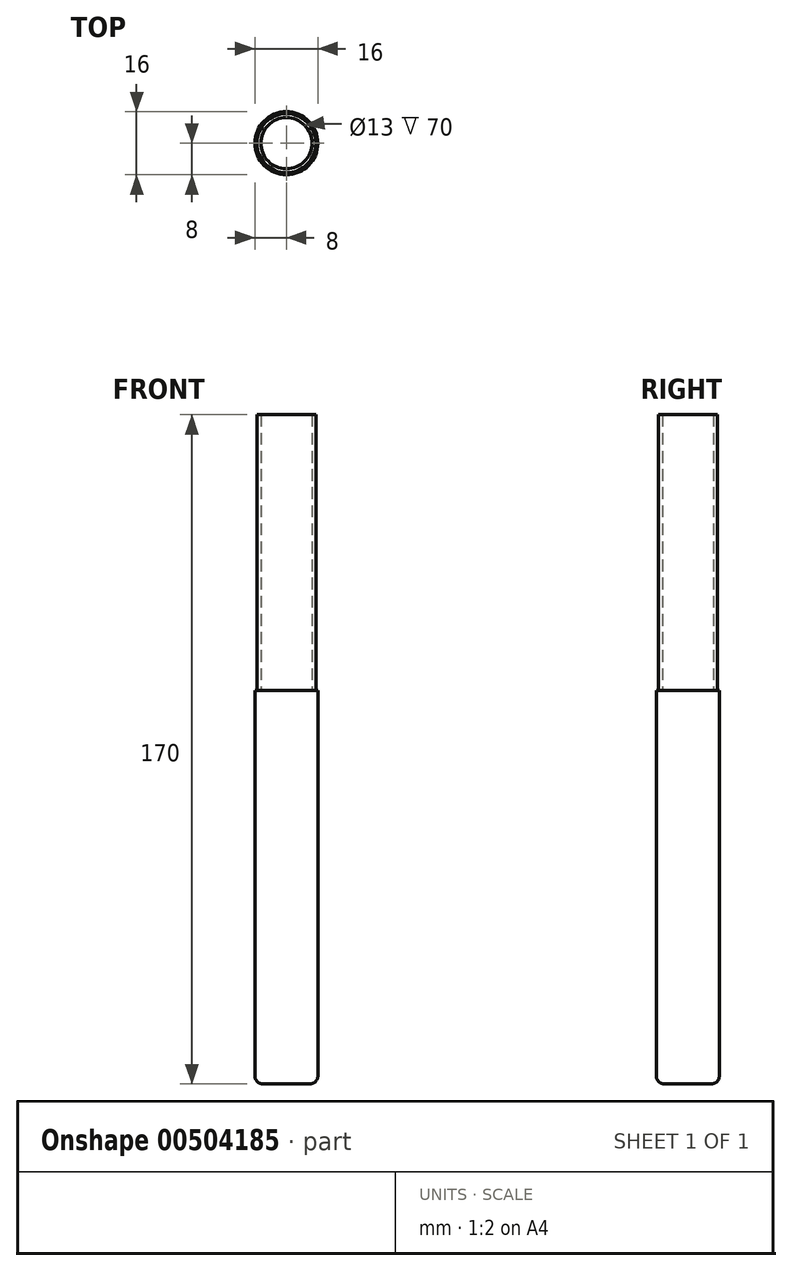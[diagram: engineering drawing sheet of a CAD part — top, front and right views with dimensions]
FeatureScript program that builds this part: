
annotation { "Feature Type Name" : "Feature", "Feature Type Description" : "" }
export const myFeature = defineFeature(function(context is Context, id is Id, definition is map)
    precondition{}
    {
        {
            var Q0;
            Q0=qCreatedBy(makeId("Top.planeOp"),FACE);
            var sketch = newSketch(context, id + "F0", { "sketchPlane" : qUnion([Q0])});
            skCircle(sketch, "E0", {"center": v(0, 0) * mm, "radius": 7.5 * mm});
            skCircle(sketch, "E1", {"center": v(0, 0) * mm, "radius": 6.5 * mm});
            skSolve(sketch);
        }
        {
            var Q0;
            Q0 = qSketchRegion(id + "F0", true);
            extrude(context, id + "F1", {"entities" : qUnion([Q0]), "depth" : 70 * mm});
        }
        {
            var Q0;
            Q0=makeQuery(id+"F1.opExtrude","CAP_FACE",FACE,{"disambiguationData":[OSD([sQuery(id+"F0.wireOp",EDGE,"E0"),sQuery(id+"F0.wireOp",EDGE,"E1")])],"isStart":true});
            var sketch = newSketch(context, id + "F2", { "sketchPlane" : qUnion([Q0])});
            skCircle(sketch, "E2", {"center": v(0, 0) * mm, "radius": 8 * mm});
            skSolve(sketch);
        }
        {
            var Q0;
            Q0 = qSketchRegion(id + "F2", true);
            extrude(context, id + "F3", {"entities" : qUnion([Q0]), "operationType" : NewBodyOperationType.ADD, "depth" : 100 * mm});
        }
        {
            var Q0;
            Q0=makeQuery(id+"F3.opExtrude","CAP_EDGE",EDGE,{"disambiguationData":[OSD([sQuery(id+"F2.wireOp",EDGE,"E2")])],"isStart":false});
            fillet(context, id + "F4", {"entities" : qUnion([Q0]), "radius" : 2 * mm, "tangentPropagation" : true, "allowEdgeOverflow" : false});
        }
    });
